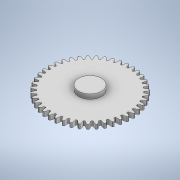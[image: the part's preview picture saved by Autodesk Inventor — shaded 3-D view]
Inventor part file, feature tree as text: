
AUTODESK INVENTOR PART (.ipt)
format: ipt  version: 2020 (Build 240168000, 168)  size: 521,216 bytes
history: native  units: mm
features: extrude x2, sketch x2, fillet x1, pattern_circular x1
ambient origin geometry x8: Origin, YZ Plane, XZ Plane, XY Plane, X Axis, Y Axis, Z Axis, Center Point
bodies: Solid1 (feature_tree)
feature tree (6):
  extrude  "Extrusion1"  Depth=3.0mm TaperAngle=360.0deg
  fillet  "Fillet2"  Radius=53.2mm
  pattern_circular  "Circular Pattern2"  [2 undecoded]
  extrude  "Extrusion3"  Depth=3.0mm
  sketch  "Sketch1"  dims[d4=3.0mm d5=0.0mm d18=430.0mm d19=360.0deg d23=53.2mm]
  sketch  "Sketch3"  dims[d25=1.546512mm d26=1.237209mm d27=3.490659mm d28=49.991647mm d29=3.490659mm d30=0.309302mm d31=0.618605mm d32=0.971704mm d33=0.4mm d34=15.0mm d35=3.0mm d36=0.0mm]
note: 2 required parameter values undecoded (feature->parameter linkage not recoverable at this tier; creation-order binding heuristic only, values carry confidence <= 0.55)
